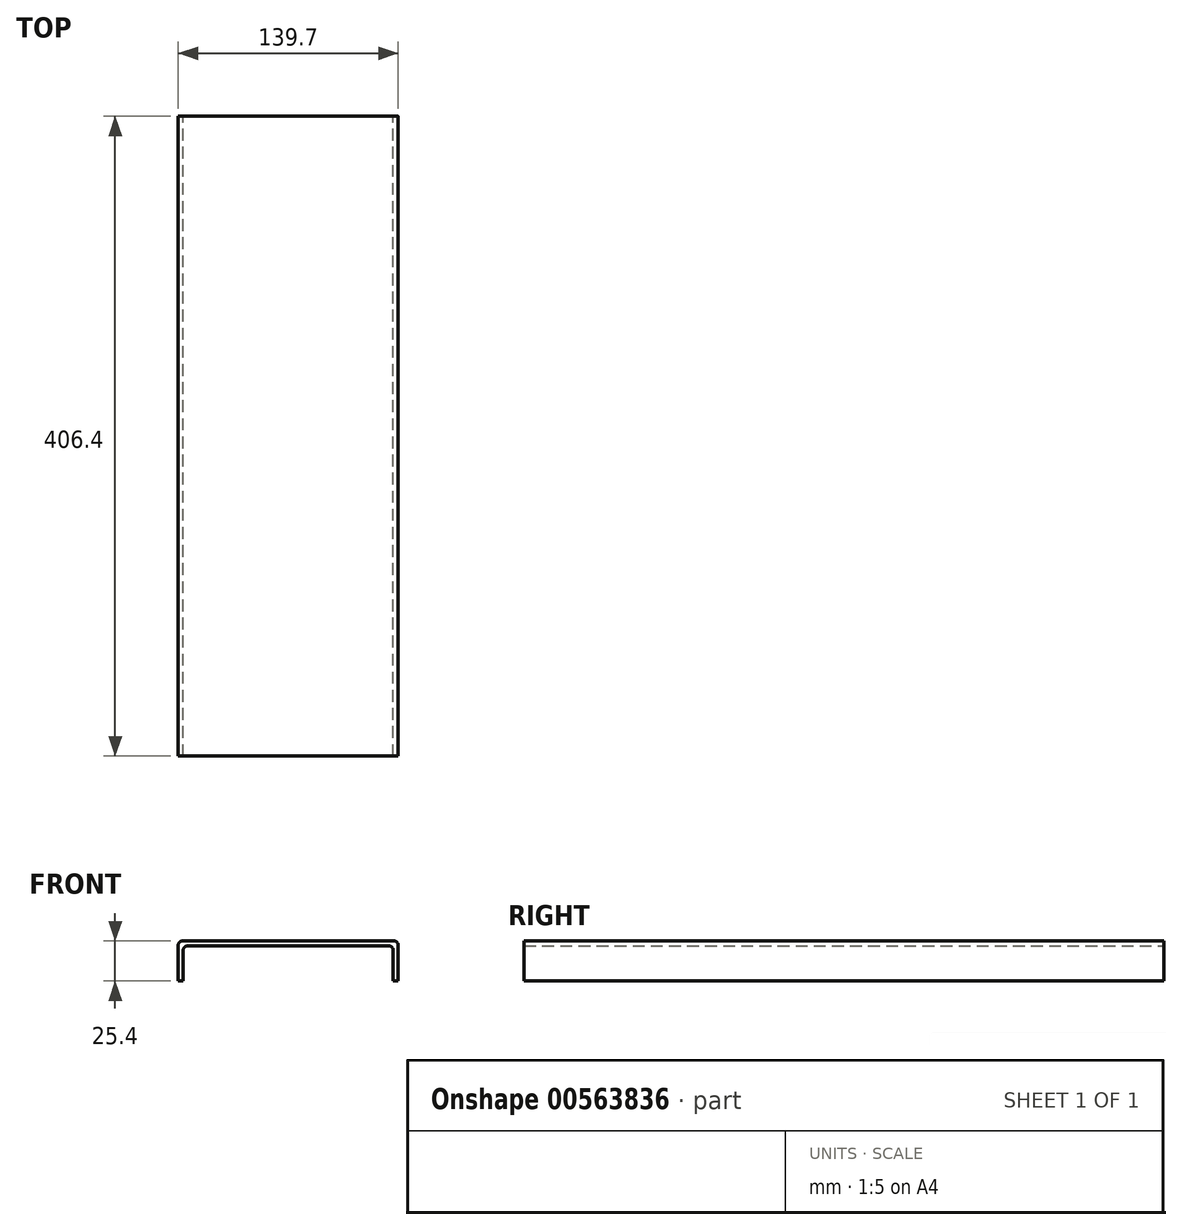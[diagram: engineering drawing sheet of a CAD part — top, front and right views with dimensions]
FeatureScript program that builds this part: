
annotation { "Feature Type Name" : "Feature", "Feature Type Description" : "" }
export const myFeature = defineFeature(function(context is Context, id is Id, definition is map)
    precondition{}
    {
        {
            var Q0;
            Q0=qCreatedBy(makeId("Front.planeOp"),FACE);
            var sketch = newSketch(context, id + "F0", { "sketchPlane" : qUnion([Q0])});
            skLineSegment(sketch, "E0.bottom", {"start": v(-69.85, 12.7) * mm, "end": v(69.85, 12.7) * mm});
            skLineSegment(sketch, "E0.top", {"start": v(-69.85, -12.7) * mm, "end": v(69.85, -12.7) * mm});
            skLineSegment(sketch, "E0.left", {"start": v(-69.85, 12.7) * mm, "end": v(-69.85, -12.7) * mm});
            skLineSegment(sketch, "E0.right", {"start": v(69.85, 12.7) * mm, "end": v(69.85, -12.7) * mm});
            skPoint(sketch, "E0.middle", {"position": v(0, 0) * mm});
            skLineSegment(sketch, "E1", {"start": v(-69.85, -12.7) * mm, "end": v(-66.68, -12.7) * mm});
            skLineSegment(sketch, "E2", {"start": v(69.85, -12.7) * mm, "end": v(66.68, -12.7) * mm});
            skLineSegment(sketch, "E3", {"start": v(66.68, -12.7) * mm, "end": v(66.68, 9.52) * mm});
            skLineSegment(sketch, "E4", {"start": v(66.68, 9.52) * mm, "end": v(-66.68, 9.52) * mm});
            skLineSegment(sketch, "E5", {"start": v(-66.68, 9.52) * mm, "end": v(-66.68, -12.7) * mm});
            skSolve(sketch);
        }
        {
            var Q0;
            Q0=makeQuery(id+"F0.imprint","IMPRINT",FACE,{"disambiguationData":[TD([[makeQuery(id+"F0.imprint","IMPRINT",EDGE,{"derivedFrom":sQuery(id+"F0.wireOp",EDGE,"E0.bottom")}),-1.0]])]});
            extrude(context, id + "F1", {"entities" : qUnion([Q0]), "endBound" : BoundingType.SYMMETRIC, "depth" : 406.4 * mm, "offsetDistance" : 25.4 * mm});
        }
        {
            var Q0;
            Q0=makeQuery(id+"F1.opExtrude","SWEPT_EDGE",EDGE,{"disambiguationData":[OSD([sQuery(id+"F0.wireOp",EDGE,"E0.bottom"),sQuery(id+"F0.wireOp",EDGE,"E0.left")])]});
            var Q1;
            Q1=makeQuery(id+"F1.opExtrude","SWEPT_EDGE",EDGE,{"disambiguationData":[OSD([sQuery(id+"F0.wireOp",EDGE,"E0.bottom"),sQuery(id+"F0.wireOp",EDGE,"E0.right")])]});
            fillet(context, id + "F2", {"entities" : qUnion([Q0, Q1]), "radius" : 2.54 * mm, "tangentPropagation" : true, "allowEdgeOverflow" : false});
        }
        {
            var Q0;
            Q0=makeQuery(id+"F1.opExtrude","SWEPT_EDGE",EDGE,{"disambiguationData":[OSD([sQuery(id+"F0.wireOp",EDGE,"E4"),sQuery(id+"F0.wireOp",EDGE,"E5")])]});
            var Q1;
            Q1=makeQuery(id+"F1.opExtrude","SWEPT_EDGE",EDGE,{"disambiguationData":[OSD([sQuery(id+"F0.wireOp",EDGE,"E3"),sQuery(id+"F0.wireOp",EDGE,"E4")])]});
            fillet(context, id + "F3", {"entities" : qUnion([Q0, Q1]), "radius" : 2.54 * mm, "tangentPropagation" : true, "allowEdgeOverflow" : false});
        }
    });
